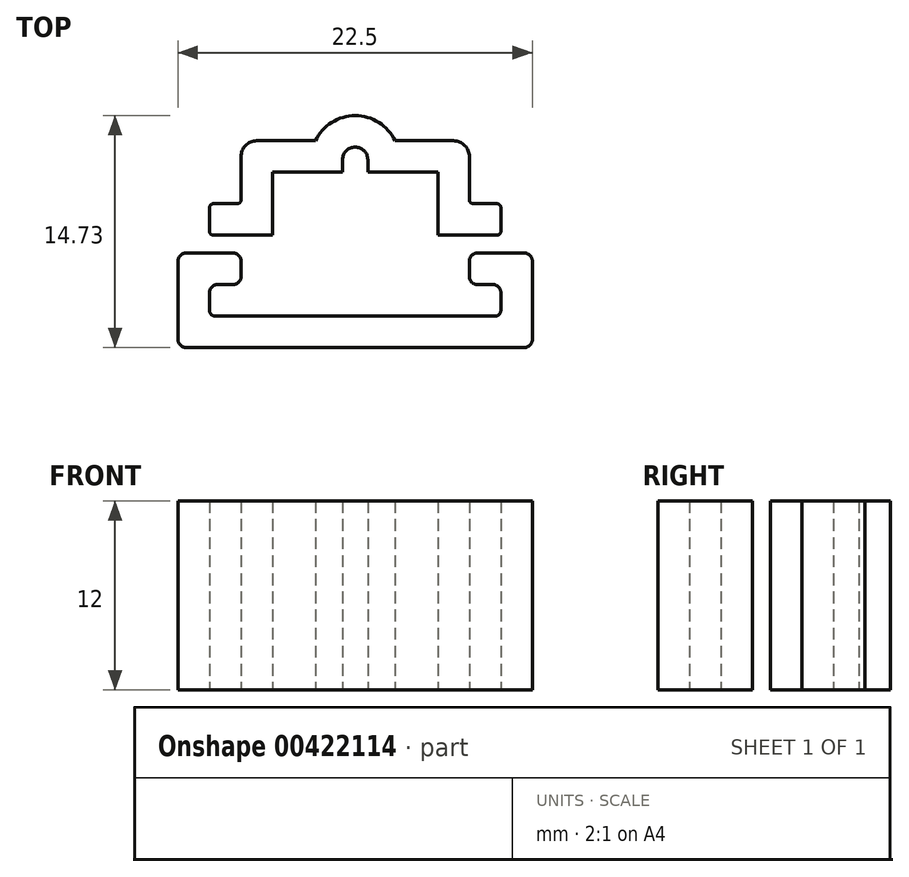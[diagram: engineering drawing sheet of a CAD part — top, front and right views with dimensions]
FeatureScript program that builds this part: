
annotation { "Feature Type Name" : "Feature", "Feature Type Description" : "" }
export const myFeature = defineFeature(function(context is Context, id is Id, definition is map)
    precondition{}
    {
        {
            var Q0;
            Q0=qCreatedBy(makeId("Top.planeOp"),FACE);
            var sketch = newSketch(context, id + "F0", { "sketchPlane" : qUnion([Q0])});
            skLineSegment(sketch, "E0.top", {"start": v(-9, 6.7) * mm, "end": v(-4.56, 6.7) * mm});
            skLineSegment(sketch, "E0.left", {"start": v(-9, 2.7) * mm, "end": v(-9, 6.7) * mm});
            skArc(sketch, "E1", {"start": v(-3.76, 8.3) * mm, "mid": v(-4.32, 8.06) * mm, "end": v(-4.56, 7.5) * mm});
            skLineSegment(sketch, "E2", {"start": v(-4.56, 6.7) * mm, "end": v(-4.56, 7.5) * mm});
            skLineSegment(sketch, "E3.1", {"start": v(-11, 4.7) * mm, "end": v(-11, 8.7) * mm});
            skLineSegment(sketch, "E3.2", {"start": v(-11, 8.7) * mm, "end": v(-6.29, 8.7) * mm});
            skArc(sketch, "E3.3", {"start": v(-3.76, 10.3) * mm, "mid": v(-5.25, 9.86) * mm, "end": v(-6.29, 8.7) * mm});
            skLineSegment(sketch, "E4", {"start": v(-9, 2.7) * mm, "end": v(-11, 2.7) * mm});
            skLineSegment(sketch, "E5", {"start": v(-13, 2.7) * mm, "end": v(-13, 4.7) * mm});
            skLineSegment(sketch, "E6", {"start": v(-13, 4.7) * mm, "end": v(-11, 4.7) * mm});
            skLineSegment(sketch, "E7", {"start": v(-13, 2.7) * mm, "end": v(-11, 2.7) * mm});
            skPoint(sketch, "E8.visualSharp", {"position": v(-13, 4.7) * mm});
            skLineSegment(sketch, "E8.filletArc", {"start": v(-13, 4.7) * mm, "end": v(-13, 4.7) * mm});
            skPoint(sketch, "E9.visualSharp", {"position": v(-13, 2.7) * mm});
            skLineSegment(sketch, "E9.filletArc", {"start": v(-13, 2.7) * mm, "end": v(-13, 2.7) * mm});
            skPoint(sketch, "E10.visualSharp", {"position": v(-11, 8.7) * mm});
            skLineSegment(sketch, "E10.filletArc", {"start": v(-11, 8.7) * mm, "end": v(-11, 8.7) * mm});
            skPoint(sketch, "E11.visualSharp", {"position": v(-11, 4.7) * mm});
            skLineSegment(sketch, "E11.filletArc", {"start": v(-11, 4.7) * mm, "end": v(-11, 4.7) * mm});
            skLineSegment(sketch, "E12", {"start": v(-3.76, 7.5) * mm, "end": v(-3.76, 10.3) * mm, "construction": true});
            skLineSegment(sketch, "E13.MirrorCS", {"start": v(3.5, 4.7) * mm, "end": v(3.5, 4.7) * mm});
            skLineSegment(sketch, "E14.MirrorCS", {"start": v(5.5, 4.7) * mm, "end": v(5.5, 4.7) * mm});
            skLineSegment(sketch, "E15.MirrorCS", {"start": v(5.5, 2.7) * mm, "end": v(5.5, 2.7) * mm});
            skLineSegment(sketch, "E16.MirrorCS", {"start": v(3.5, 8.7) * mm, "end": v(3.5, 8.7) * mm});
            skArc(sketch, "E17.MirrorCS", {"start": v(-4.56, 7.5) * mm, "mid": v(-3.76, 8.3) * mm, "end": v(-2.96, 7.5) * mm});
            skLineSegment(sketch, "E18.MirrorCS", {"start": v(-2.96, 6.7) * mm, "end": v(-2.96, 7.5) * mm});
            skLineSegment(sketch, "E19.MirrorCS", {"start": v(1.5, 2.7) * mm, "end": v(1.5, 6.7) * mm});
            skLineSegment(sketch, "E20.MirrorCS", {"start": v(3.5, 4.7) * mm, "end": v(3.5, 8.7) * mm});
            skLineSegment(sketch, "E21.MirrorCS", {"start": v(1.5, 6.7) * mm, "end": v(-2.96, 6.7) * mm});
            skLineSegment(sketch, "E22.MirrorCS", {"start": v(3.5, 8.7) * mm, "end": v(-1.23, 8.7) * mm});
            skArc(sketch, "E23.MirrorCS", {"start": v(-3.76, 10.3) * mm, "mid": v(-2.26, 9.86) * mm, "end": v(-1.23, 8.7) * mm});
            skLineSegment(sketch, "E24.MirrorCS", {"start": v(1.5, 2.7) * mm, "end": v(3.5, 2.7) * mm});
            skLineSegment(sketch, "E25.MirrorCS", {"start": v(5.5, 2.7) * mm, "end": v(5.5, 4.7) * mm});
            skLineSegment(sketch, "E26.MirrorCS", {"start": v(5.5, 2.7) * mm, "end": v(3.5, 2.7) * mm});
            skLineSegment(sketch, "E27.MirrorCS", {"start": v(5.5, 4.7) * mm, "end": v(3.5, 4.7) * mm});
            skLineSegment(sketch, "E28", {"start": v(-3.76, -2.44) * mm, "end": v(-13, -2.44) * mm});
            skLineSegment(sketch, "E29", {"start": v(-13, -2.44) * mm, "end": v(-13, -0.44) * mm});
            skLineSegment(sketch, "E30", {"start": v(-13, -0.44) * mm, "end": v(-11, -0.44) * mm});
            skPoint(sketch, "E31.visualSharp", {"position": v(-13, -0.44) * mm});
            skLineSegment(sketch, "E31.filletArc", {"start": v(-13, -0.44) * mm, "end": v(-13, -0.44) * mm});
            skPoint(sketch, "E32.visualSharp", {"position": v(-13, -2.44) * mm});
            skLineSegment(sketch, "E32.filletArc", {"start": v(-13, -2.44) * mm, "end": v(-13, -2.44) * mm});
            skPoint(sketch, "E33.visualSharp", {"position": v(-11, -0.44) * mm});
            skLineSegment(sketch, "E33.filletArc", {"start": v(-11, -0.44) * mm, "end": v(-11, -0.44) * mm});
            skLineSegment(sketch, "E34.0", {"start": v(-15, 1.56) * mm, "end": v(-11, 1.56) * mm});
            skLineSegment(sketch, "E34.1", {"start": v(-15, -4.44) * mm, "end": v(-15, 1.56) * mm});
            skLineSegment(sketch, "E34.2", {"start": v(-3.76, -4.44) * mm, "end": v(-15, -4.44) * mm});
            skLineSegment(sketch, "E35", {"start": v(-11, 1.56) * mm, "end": v(-11, -0.44) * mm});
            skPoint(sketch, "E36.MirrorP", {"position": v(5.5, -2.44) * mm});
            skPoint(sketch, "E37.MirrorP", {"position": v(3.5, -0.44) * mm});
            skPoint(sketch, "E38.MirrorP", {"position": v(5.5, -0.44) * mm});
            skLineSegment(sketch, "E39.MirrorCS", {"start": v(5.5, -0.44) * mm, "end": v(3.5, -0.44) * mm});
            skLineSegment(sketch, "E40.MirrorCS", {"start": v(3.5, -0.44) * mm, "end": v(3.5, -0.44) * mm});
            skLineSegment(sketch, "E41.MirrorCS", {"start": v(5.5, -2.44) * mm, "end": v(5.5, -0.44) * mm});
            skLineSegment(sketch, "E42.MirrorCS", {"start": v(5.5, -2.44) * mm, "end": v(5.5, -2.44) * mm});
            skLineSegment(sketch, "E43.MirrorCS", {"start": v(3.5, 1.56) * mm, "end": v(3.5, -0.44) * mm});
            skLineSegment(sketch, "E44.MirrorCS", {"start": v(7.5, 1.56) * mm, "end": v(3.5, 1.56) * mm});
            skLineSegment(sketch, "E45.MirrorCS", {"start": v(-3.76, -2.44) * mm, "end": v(5.5, -2.44) * mm});
            skLineSegment(sketch, "E46.MirrorCS", {"start": v(-3.76, -4.44) * mm, "end": v(7.5, -4.44) * mm});
            skLineSegment(sketch, "E47.MirrorCS", {"start": v(7.5, -4.44) * mm, "end": v(7.5, 1.56) * mm});
            skLineSegment(sketch, "E48.MirrorCS", {"start": v(5.5, -0.44) * mm, "end": v(5.5, -0.44) * mm});
            skSolve(sketch);
        }
        {
            var Q0;
            Q0=makeQuery(id+"F0.imprint","IMPRINT",FACE,{"disambiguationData":[TD([[makeQuery(id+"F0.imprint","IMPRINT",EDGE,{"derivedFrom":sQuery(id+"F0.wireOp",EDGE,"E0.top")}),1.0]])]});
            var Q1;
            Q1=makeQuery(id+"F0.imprint","IMPRINT",FACE,{"disambiguationData":[TD([[makeQuery(id+"F0.imprint","IMPRINT",EDGE,{"derivedFrom":sQuery(id+"F0.wireOp",EDGE,"E28")}),1.0]])]});
            extrude(context, id + "F1", {"entities" : qUnion([Q0, Q1]), "endBound" : BoundingType.SYMMETRIC, "depth" : 12 * mm});
        }
        {
            var Q0;
            Q0=makeQuery(id+"F1.opExtrude","SWEPT_EDGE",EDGE,{"disambiguationData":[OSD([sQuery(id+"F0.wireOp",EDGE,"E3.1"),sQuery(id+"F0.wireOp",EDGE,"E3.2")])]});
            var Q1;
            Q1=makeQuery(id+"F1.opExtrude","SWEPT_EDGE",EDGE,{"disambiguationData":[OSD([sQuery(id+"F0.wireOp",EDGE,"E20.MirrorCS"),sQuery(id+"F0.wireOp",EDGE,"E22.MirrorCS")])]});
            var Q2;
            Q2=makeQuery(id+"F1.opExtrude","SWEPT_EDGE",EDGE,{"disambiguationData":[OSD([sQuery(id+"F0.wireOp",EDGE,"e1049401-0613-475a-b577-332d0adae607.1"),sQuery(id+"F0.wireOp",EDGE,"e1049401-0613-475a-b577-332d0adae607.2")])]});
            var Q3;
            Q3=makeQuery(id+"F1.opExtrude","SWEPT_EDGE",EDGE,{"disambiguationData":[OSD([sQuery(id+"F0.wireOp",EDGE,"e1049401-0613-475a-b577-332d0adae607.0"),sQuery(id+"F0.wireOp",EDGE,"e1049401-0613-475a-b577-332d0adae607.1")])]});
            var Q4;
            Q4=makeQuery(id+"F1.opExtrude","SWEPT_EDGE",EDGE,{"disambiguationData":[OSD([sQuery(id+"F0.wireOp",EDGE,"2f623f65-f567-49c9-82c0-9cb03db9aa17.MirrorCS"),sQuery(id+"F0.wireOp",EDGE,"19fd8c1c-7484-4fa6-ae31-6b80ee20e007.MirrorCS")])]});
            var Q5;
            Q5=makeQuery(id+"F1.opExtrude","SWEPT_EDGE",EDGE,{"disambiguationData":[OSD([sQuery(id+"F0.wireOp",EDGE,"96f65a23-e4fa-4baa-86ae-8c059f4698ef.MirrorCS"),sQuery(id+"F0.wireOp",EDGE,"19fd8c1c-7484-4fa6-ae31-6b80ee20e007.MirrorCS")])]});
            var Q6;
            Q6=makeQuery(id+"F1.opExtrude","SWEPT_EDGE",EDGE,{"disambiguationData":[OSD([sQuery(id+"F0.wireOp",EDGE,"60dc2f18-db31-43ca-8e62-799d7e8ac6f97.MirrorCS"),sQuery(id+"F0.wireOp",EDGE,"60dc2f18-db31-43ca-8e62-799d7e8ac6f99.MirrorCS")])]});
            var Q7;
            Q7=makeQuery(id+"F1.opExtrude","SWEPT_EDGE",EDGE,{"disambiguationData":[OSD([sQuery(id+"F0.wireOp",EDGE,"60dc2f18-db31-43ca-8e62-799d7e8ac6f99.MirrorCS"),sQuery(id+"F0.wireOp",EDGE,"60dc2f18-db31-43ca-8e62-799d7e8ac6f911.MirrorCS")])]});
            fillet(context, id + "F2", {"entities" : qUnion([Q0, Q1, Q2, Q3, Q4, Q5, Q6, Q7]), "radius" : 1 * mm, "tangentPropagation" : true, "allowEdgeOverflow" : false});
        }
        {
            var Q0;
            Q0=makeQuery(id+"F1.opExtrude","SWEPT_EDGE",EDGE,{"disambiguationData":[OSD([sQuery(id+"F0.wireOp",EDGE,"E3.1"),sQuery(id+"F0.wireOp",EDGE,"E6")])]});
            var Q1;
            Q1=makeQuery(id+"F1.opExtrude","SWEPT_EDGE",EDGE,{"disambiguationData":[OSD([sQuery(id+"F0.wireOp",EDGE,"E5"),sQuery(id+"F0.wireOp",EDGE,"E6")])]});
            var Q2;
            Q2=makeQuery(id+"F1.opExtrude","SWEPT_EDGE",EDGE,{"disambiguationData":[OSD([sQuery(id+"F0.wireOp",EDGE,"E5"),sQuery(id+"F0.wireOp",EDGE,"E7")])]});
            var Q3;
            Q3=makeQuery(id+"F1.opExtrude","SWEPT_EDGE",EDGE,{"disambiguationData":[OSD([sQuery(id+"F0.wireOp",EDGE,"E20.MirrorCS"),sQuery(id+"F0.wireOp",EDGE,"E27.MirrorCS")])]});
            var Q4;
            Q4=makeQuery(id+"F1.opExtrude","SWEPT_EDGE",EDGE,{"disambiguationData":[OSD([sQuery(id+"F0.wireOp",EDGE,"E25.MirrorCS"),sQuery(id+"F0.wireOp",EDGE,"E27.MirrorCS")])]});
            var Q5;
            Q5=makeQuery(id+"F1.opExtrude","SWEPT_EDGE",EDGE,{"disambiguationData":[OSD([sQuery(id+"F0.wireOp",EDGE,"E25.MirrorCS"),sQuery(id+"F0.wireOp",EDGE,"E26.MirrorCS")])]});
            fillet(context, id + "F3", {"entities" : qUnion([Q0, Q1, Q2, Q3, Q4, Q5]), "radius" : 0.25 * mm, "tangentPropagation" : true, "allowEdgeOverflow" : false});
        }
        {
            var Q0;
            Q0=makeQuery(id+"F1.opExtrude","SWEPT_EDGE",EDGE,{"disambiguationData":[OSD([sQuery(id+"F0.wireOp",EDGE,"e1049401-0613-475a-b577-332d0adae607.0"),sQuery(id+"F0.wireOp",EDGE,"984c04f7-a5d2-4a6d-bb31-1cf7d886feb0")])]});
            var Q1;
            Q1=makeQuery(id+"F1.opExtrude","SWEPT_EDGE",EDGE,{"disambiguationData":[OSD([sQuery(id+"F0.wireOp",EDGE,"E30"),sQuery(id+"F0.wireOp",EDGE,"984c04f7-a5d2-4a6d-bb31-1cf7d886feb0")])]});
            var Q2;
            Q2=makeQuery(id+"F1.opExtrude","SWEPT_EDGE",EDGE,{"disambiguationData":[OSD([sQuery(id+"F0.wireOp",EDGE,"2f623f65-f567-49c9-82c0-9cb03db9aa17.MirrorCS"),sQuery(id+"F0.wireOp",EDGE,"a718e26f-6de6-4fa9-8099-4ff6b175679c.MirrorCS")])]});
            var Q3;
            Q3=makeQuery(id+"F1.opExtrude","SWEPT_EDGE",EDGE,{"disambiguationData":[OSD([sQuery(id+"F0.wireOp",EDGE,"a718e26f-6de6-4fa9-8099-4ff6b175679c.MirrorCS"),sQuery(id+"F0.wireOp",EDGE,"4dffd293-6893-4055-826d-da92bf63a32f.MirrorCS")])]});
            var Q4;
            Q4=makeQuery(id+"F1.opExtrude","SWEPT_EDGE",EDGE,{"disambiguationData":[OSD([sQuery(id+"F0.wireOp",EDGE,"60dc2f18-db31-43ca-8e62-799d7e8ac6f914.MirrorCS"),sQuery(id+"F0.wireOp",EDGE,"60dc2f18-db31-43ca-8e62-799d7e8ac6f917.MirrorCS")])]});
            var Q5;
            Q5=makeQuery(id+"F1.opExtrude","SWEPT_EDGE",EDGE,{"disambiguationData":[OSD([sQuery(id+"F0.wireOp",EDGE,"60dc2f18-db31-43ca-8e62-799d7e8ac6f97.MirrorCS"),sQuery(id+"F0.wireOp",EDGE,"60dc2f18-db31-43ca-8e62-799d7e8ac6f914.MirrorCS")])]});
            var Q6;
            Q6=makeQuery(id+"F1.opExtrude","SWEPT_EDGE",EDGE,{"disambiguationData":[OSD([sQuery(id+"F0.wireOp",EDGE,"E39.MirrorCS"),sQuery(id+"F0.wireOp",EDGE,"E43.MirrorCS")])]});
            var Q7;
            Q7=makeQuery(id+"F1.opExtrude","SWEPT_EDGE",EDGE,{"disambiguationData":[OSD([sQuery(id+"F0.wireOp",EDGE,"E39.MirrorCS"),sQuery(id+"F0.wireOp",EDGE,"E41.MirrorCS")])]});
            var Q8;
            Q8=makeQuery(id+"F1.opExtrude","SWEPT_EDGE",EDGE,{"disambiguationData":[OSD([sQuery(id+"F0.wireOp",EDGE,"E34.0"),sQuery(id+"F0.wireOp",EDGE,"E35")])]});
            var Q9;
            Q9=makeQuery(id+"F1.opExtrude","SWEPT_EDGE",EDGE,{"disambiguationData":[OSD([sQuery(id+"F0.wireOp",EDGE,"E43.MirrorCS"),sQuery(id+"F0.wireOp",EDGE,"E44.MirrorCS")])]});
            var Q10;
            Q10=makeQuery(id+"F1.opExtrude","SWEPT_EDGE",EDGE,{"disambiguationData":[OSD([sQuery(id+"F0.wireOp",EDGE,"E34.0"),sQuery(id+"F0.wireOp",EDGE,"E34.1")])]});
            var Q11;
            Q11=makeQuery(id+"F1.opExtrude","SWEPT_EDGE",EDGE,{"disambiguationData":[OSD([sQuery(id+"F0.wireOp",EDGE,"E44.MirrorCS"),sQuery(id+"F0.wireOp",EDGE,"E47.MirrorCS")])]});
            var Q12;
            Q12=makeQuery(id+"F1.opExtrude","SWEPT_EDGE",EDGE,{"disambiguationData":[OSD([sQuery(id+"F0.wireOp",EDGE,"E34.1"),sQuery(id+"F0.wireOp",EDGE,"E34.2")])]});
            var Q13;
            Q13=makeQuery(id+"F1.opExtrude","SWEPT_EDGE",EDGE,{"disambiguationData":[OSD([sQuery(id+"F0.wireOp",EDGE,"E46.MirrorCS"),sQuery(id+"F0.wireOp",EDGE,"E47.MirrorCS")])]});
            fillet(context, id + "F4", {"entities" : qUnion([Q0, Q1, Q2, Q3, Q4, Q5, Q6, Q7, Q8, Q9, Q10, Q11, Q12, Q13]), "radius" : 0.5 * mm, "tangentPropagation" : true, "allowEdgeOverflow" : false});
        }
        {
            var Q0;
            Q0=makeQuery(id+"F1.opExtrude","SWEPT_EDGE",EDGE,{"disambiguationData":[OSD([sQuery(id+"F0.wireOp",EDGE,"E29"),sQuery(id+"F0.wireOp",EDGE,"E30")])]});
            var Q1;
            Q1=makeQuery(id+"F1.opExtrude","SWEPT_EDGE",EDGE,{"disambiguationData":[OSD([sQuery(id+"F0.wireOp",EDGE,"E28"),sQuery(id+"F0.wireOp",EDGE,"E29")])]});
            var Q2;
            Q2=makeQuery(id+"F1.opExtrude","SWEPT_EDGE",EDGE,{"disambiguationData":[OSD([sQuery(id+"F0.wireOp",EDGE,"22189d52-49ab-4dfe-9d21-857200e26c20.MirrorCS"),sQuery(id+"F0.wireOp",EDGE,"fa9916d5-57d3-459e-8d3c-f4e265bd6564.MirrorCS")])]});
            var Q3;
            Q3=makeQuery(id+"F1.opExtrude","SWEPT_EDGE",EDGE,{"disambiguationData":[OSD([sQuery(id+"F0.wireOp",EDGE,"22189d52-49ab-4dfe-9d21-857200e26c20.MirrorCS"),sQuery(id+"F0.wireOp",EDGE,"4dffd293-6893-4055-826d-da92bf63a32f.MirrorCS")])]});
            var Q4;
            Q4=makeQuery(id+"F1.opExtrude","SWEPT_EDGE",EDGE,{"disambiguationData":[OSD([sQuery(id+"F0.wireOp",EDGE,"60dc2f18-db31-43ca-8e62-799d7e8ac6f96.MirrorCS"),sQuery(id+"F0.wireOp",EDGE,"60dc2f18-db31-43ca-8e62-799d7e8ac6f915.MirrorCS")])]});
            var Q5;
            Q5=makeQuery(id+"F1.opExtrude","SWEPT_EDGE",EDGE,{"disambiguationData":[OSD([sQuery(id+"F0.wireOp",EDGE,"60dc2f18-db31-43ca-8e62-799d7e8ac6f915.MirrorCS"),sQuery(id+"F0.wireOp",EDGE,"60dc2f18-db31-43ca-8e62-799d7e8ac6f917.MirrorCS")])]});
            var Q6;
            Q6=makeQuery(id+"F1.opExtrude","SWEPT_EDGE",EDGE,{"disambiguationData":[OSD([sQuery(id+"F0.wireOp",EDGE,"E41.MirrorCS"),sQuery(id+"F0.wireOp",EDGE,"E45.MirrorCS")])]});
            fillet(context, id + "F5", {"entities" : qUnion([Q0, Q1, Q2, Q3, Q4, Q5, Q6]), "radius" : 0.35 * mm, "tangentPropagation" : true, "allowEdgeOverflow" : false});
        }
    });
